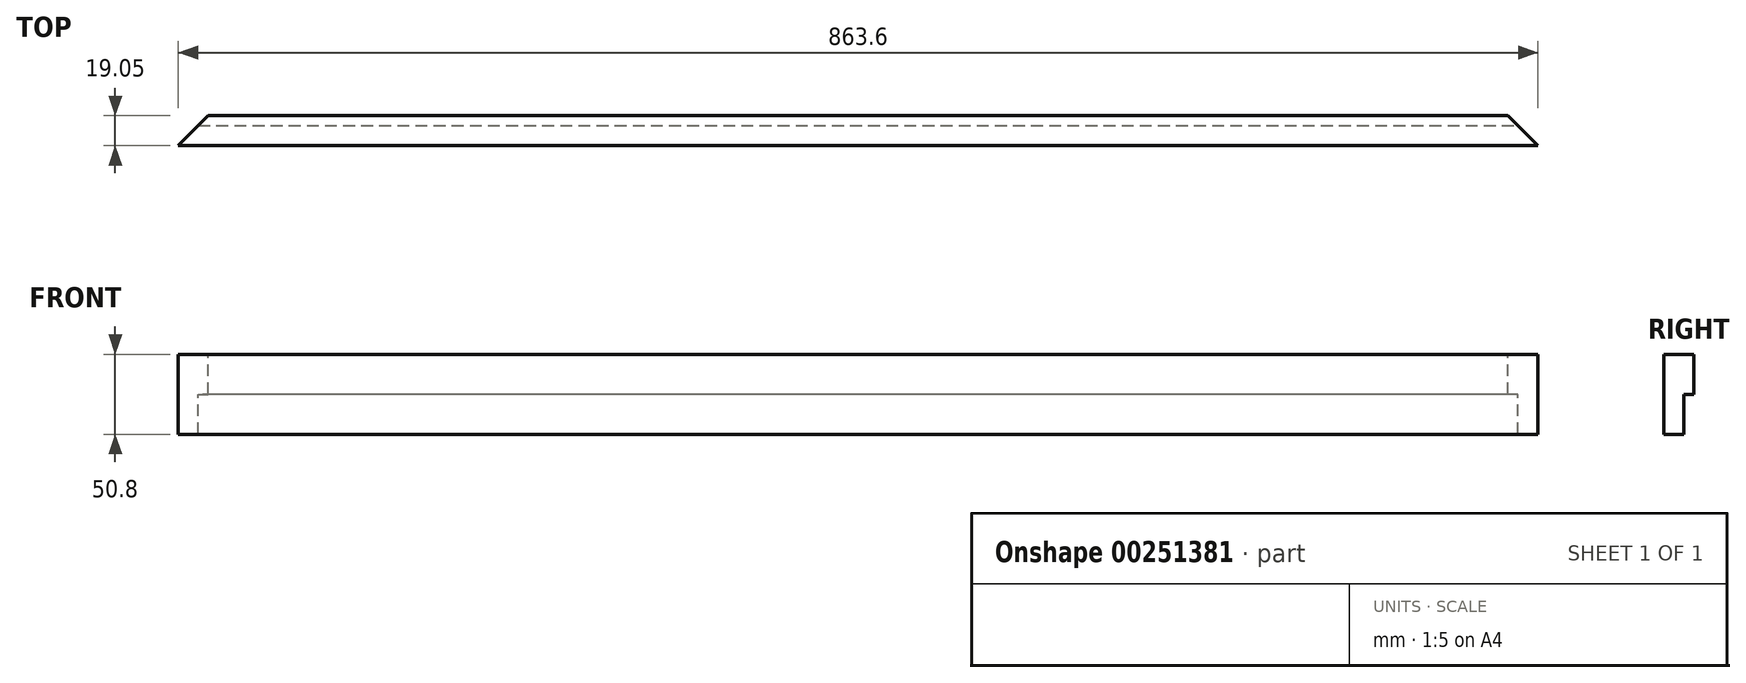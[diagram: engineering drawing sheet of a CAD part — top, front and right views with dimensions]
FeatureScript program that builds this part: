
annotation { "Feature Type Name" : "Feature", "Feature Type Description" : "" }
export const myFeature = defineFeature(function(context is Context, id is Id, definition is map)
    precondition{}
    {
        {
            var Q0;
            Q0=qCreatedBy(makeId("Front.planeOp"),FACE);
            var sketch = newSketch(context, id + "F0", { "sketchPlane" : qUnion([Q0])});
            skLineSegment(sketch, "E0.bottom", {"start": v(-381, 25.4) * mm, "end": v(381, 25.4) * mm});
            skLineSegment(sketch, "E0.top", {"start": v(-381, -25.4) * mm, "end": v(381, -25.4) * mm});
            skLineSegment(sketch, "E0.left", {"start": v(-381, 25.4) * mm, "end": v(-381, -25.4) * mm});
            skLineSegment(sketch, "E0.right", {"start": v(381, 25.4) * mm, "end": v(381, -25.4) * mm});
            skPoint(sketch, "E0.middle", {"position": v(0, 0) * mm});
            skSolve(sketch);
        }
        {
            var Q0;
            Q0 = qSketchRegion(id + "F0", true);
            extrude(context, id + "F1", {"entities" : qUnion([Q0]), "depth" : 19.05 * mm});
        }
        {
            var Q0;
            Q0=makeQuery(id+"F1.opExtrude","SWEPT_FACE",FACE,{"disambiguationData":[OSD([sQuery(id+"F0.wireOp",EDGE,"E0.left")])]});
            var sketch = newSketch(context, id + "F2", { "sketchPlane" : qUnion([Q0])});
            skLineSegment(sketch, "E1", {"start": v(19.05, -25.4) * mm, "end": v(6.35, -25.4) * mm});
            skLineSegment(sketch, "E2", {"start": v(6.35, -25.4) * mm, "end": v(6.35, 0) * mm});
            skLineSegment(sketch, "E3", {"start": v(6.35, 0) * mm, "end": v(0, 0) * mm});
            skLineSegment(sketch, "E4", {"start": v(0, 0) * mm, "end": v(-13, 0) * mm});
            skLineSegment(sketch, "E5", {"start": v(-13, 0) * mm, "end": v(-13, -29.99) * mm});
            skLineSegment(sketch, "E6", {"start": v(-13, -29.99) * mm, "end": v(6.35, -29.99) * mm});
            skLineSegment(sketch, "E7", {"start": v(6.35, -29.99) * mm, "end": v(6.35, -25.4) * mm});
            skSolve(sketch);
        }
        {
            var Q0;
            Q0 = qSketchRegion(id + "F2", true);
            extrude(context, id + "F3", {"entities" : qUnion([Q0]), "operationType" : NewBodyOperationType.REMOVE, "endBound" : BoundingType.THROUGH_ALL, "oppositeDirection" : true, "depth" : 25.4 * mm});
        }
        {
            var Q0;
            Q0=makeQuery(id+"F1.opExtrude","SWEPT_FACE",FACE,{"disambiguationData":[OSD([sQuery(id+"F0.wireOp",EDGE,"E0.left")])]});
            extrude(context, id + "F4", {"entities" : qUnion([Q0]), "operationType" : NewBodyOperationType.ADD, "depth" : 50.8 * mm});
        }
        {
            var Q0;
            Q0=makeQuery(id+"F1.opExtrude","SWEPT_FACE",FACE,{"disambiguationData":[OSD([sQuery(id+"F0.wireOp",EDGE,"E0.right")])]});
            extrude(context, id + "F5", {"entities" : qUnion([Q0]), "operationType" : NewBodyOperationType.ADD, "depth" : 50.8 * mm});
        }
        {
            var Q0;
            {var subQ0=sQuery(id+"F0.wireOp",EDGE,"E0.bottom");Q0=makeQuery(id+"F5.boolean.opBoolean","MERGE",FACE,{"derivedFrom":[makeQuery(id+"F4.boolean.opBoolean","MERGE",FACE,{"derivedFrom":[makeQuery(id+"F1.opExtrude","SWEPT_FACE",FACE,{"disambiguationData":[OSD([subQ0])]}),makeQuery(id+"F4.opExtrude","SWEPT_FACE",FACE,{"disambiguationData":[OSD([subQ0,sQuery(id+"F0.wireOp",EDGE,"E0.left")])]})]}),makeQuery(id+"F5.opExtrude","SWEPT_FACE",FACE,{"disambiguationData":[OSD([subQ0,sQuery(id+"F0.wireOp",EDGE,"E0.right")])]})]});}
            var sketch = newSketch(context, id + "F6", { "sketchPlane" : qUnion([Q0])});
            skLineSegment(sketch, "E8", {"start": v(431.8, -19.05) * mm, "end": v(412.75, 0) * mm});
            skLineSegment(sketch, "E9", {"start": v(412.75, 0) * mm, "end": v(412.75, 9.31) * mm});
            skLineSegment(sketch, "E10", {"start": v(412.75, 9.31) * mm, "end": v(436.45, 9.31) * mm});
            skLineSegment(sketch, "E11", {"start": v(436.45, 9.31) * mm, "end": v(436.45, -19.05) * mm});
            skLineSegment(sketch, "E12", {"start": v(436.45, -19.05) * mm, "end": v(431.8, -19.05) * mm});
            skLineSegment(sketch, "E13", {"start": v(-431.8, -19.05) * mm, "end": v(-412.75, 0) * mm});
            skLineSegment(sketch, "E14", {"start": v(-412.75, 0) * mm, "end": v(-412.75, 9.48) * mm});
            skLineSegment(sketch, "E15", {"start": v(-412.75, 9.48) * mm, "end": v(-444.39, 9.48) * mm});
            skLineSegment(sketch, "E16", {"start": v(-444.39, 9.48) * mm, "end": v(-444.39, -19.05) * mm});
            skLineSegment(sketch, "E17", {"start": v(-444.39, -19.05) * mm, "end": v(-431.8, -19.05) * mm});
            skSolve(sketch);
        }
        {
            var Q0;
            Q0 = qSketchRegion(id + "F6", true);
            extrude(context, id + "F7", {"entities" : qUnion([Q0]), "operationType" : NewBodyOperationType.REMOVE, "endBound" : BoundingType.THROUGH_ALL, "oppositeDirection" : true, "depth" : 25.4 * mm});
        }
    });
